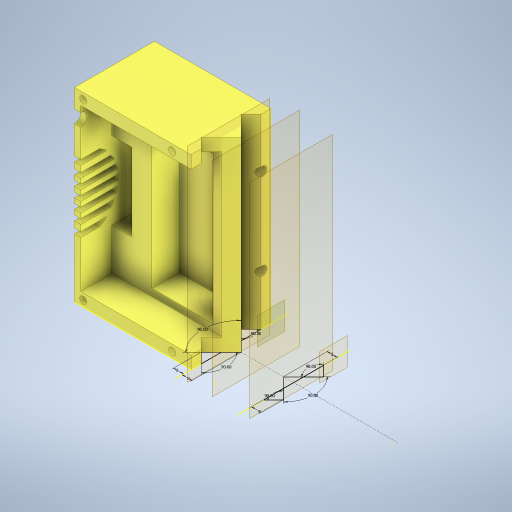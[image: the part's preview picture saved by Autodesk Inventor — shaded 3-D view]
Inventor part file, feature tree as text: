
AUTODESK INVENTOR PART (.ipt)
format: ipt  version: 2023 (Build 270158030, 158C)  size: 766,464 bytes
history: native  units: mm
features: sketch x21, extrude x18, hole x7, projected_geometry x7, plane x4, mirror x2, split x1
ambient origin geometry x8: Origin, YZ Plane, XZ Plane, XY Plane, X Axis, Y Axis, Z Axis, Center Point
bodies: Solid1 (feature_tree)
feature tree (60):
  extrude  "MainInnerBodyExtrusion"  Depth=149.0mm
  extrude  "HoleForCamerabase"  Depth=50.0mm
  extrude  "HoleForFan"  Depth=54.0mm
  extrude  "HoleForPi"  TaperAngle=0.0deg  [1 undecoded]
  extrude  "HoleForPoeAdapter"  Depth=62.0mm
  extrude  "HoleForThermister"  Depth=47.0mm
  extrude  "HoleForSensor"  Depth=32.0mm
  extrude  "SlotsForRearFan"  Depth=47.0mm
  extrude  "VentForCamera"  Depth=16.0mm
  extrude  "HoleForLens"  Depth=118.0mm
  sketch  "Sketch23"  dims[d26=49.0mm d27=118.0mm]
  hole  "Hole for 6-32 Insert"  [1 undecoded]
  hole  "Screw hole for 6-32 screw"  [1 undecoded]
  hole  "Side hole for 1-4 20 insert"  [1 undecoded]
  mirror  "Mirror for side insert"
  extrude  "Extrusion18"  Depth=17.0mm
  extrude  "HoleForPowerWire"  TaperAngle=0.0deg  [1 undecoded]
  extrude  "Extrusion22"  Depth=2.0mm
  extrude  "Extrusion23"  Depth=4.0mm
  extrude  "ExtrusionForBottom"  Depth=4.0mm
  hole  "1-4 holesToBoltFixture"  [1 undecoded]
  plane  "Work Plane1"
  plane  "Work Plane2"
  mirror  "Mirror4"
  extrude  "CutOutForFilter"  Depth=22.0mm
  hole  "Hole13"  [1 undecoded]
  plane  "Work Plane4"
  hole  "Hole14"  [1 undecoded]
  plane  "Work Plane5"
  hole  "Hole15"  [1 undecoded]
  split  "Split8"
  sketch  "Sketch46"  dims[d73=4.0mm d75=4.0mm]
  extrude  "Extrusion33"  Depth=149.0mm
  extrude  "Extrusion34"  Depth=149.0mm
  sketch  "Sketch1"  dims[d0=222.7mm d1=149.0mm]
  sketch  "Sketch3"  dims[d2=50.0mm d3=0.0mm d5=15.7mm]
  sketch  "Sketch4"  dims[d6=54.0mm d7=59.0mm]
  sketch  "Sketch6"  dims[d8=47.0mm d9=0.0mm]
  sketch  "Sketch7"  dims[d13=16.0mm d14=62.0mm]
  sketch  "Sketch11"  dims[d15=3.0mm d16=47.0mm]
  sketch  "Sketch15"  dims[d17=0.0mm d20=32.0mm]
  sketch  "Sketch16"  dims[d21=129.0mm d22=47.0mm]
  sketch  "Sketch18"  dims[d23=0.0mm d25=16.0mm]
  sketch  "Sketch24"  dims[d28=47.0mm d29=0.0mm]
  sketch  "Sketch25"  dims[d36=69.0mm d37=28.0mm]
  projected_geometry  "Projected Loop1"
  sketch  "Sketch26"  dims[d38=47.0mm d39=0.0mm]
  sketch  "Sketch37"  dims[d42=50.0mm d43=17.0mm]
  projected_geometry  "Projected Loop3"
  projected_geometry  "Projected Loop4"
  sketch  "Sketch39"  dims[d46=31.5mm d47=0.0mm]
  projected_geometry  "Projected Loop5"
  sketch  "Sketch40"  dims[d67=60.0mm d69=2.0mm]
  sketch  "Sketch43"  dims[d71=4.0mm d72=4.0mm]
  projected_geometry  "Projected Loop8"
  projected_geometry  "Projected Loop11"
  sketch  "Sketch47"  dims[d76=10.0mm d77=0.0mm d78=15.5mm]
  projected_geometry  "Projected Loop12"
  sketch  "Sketch48"  dims[d79=22.0mm d85=3.0mm]
  sketch  "Sketch50"  dims[d86=3.0mm d87=10.0mm d88=16.0mm d89=1.5mm d90=3.0mm d91=3.0mm d92=3.0mm d93=0.0mm d94=0.0mm d95=15.0mm d97=16.0mm d98=10.0mm d99=0.0mm d106=5.0mm d108=5.0mm d109=4.7mm d110=6.0mm d111=5.54mm d112=5.55mm d113=90.0deg d114=7.2mm d115=20.594885mm d116=3.797mm d117=6.0mm d118=12.7mm d119=2.362mm d120=90.0deg d121=15.0mm d122=20.594885mm d130=7.666mm d131=6.0mm d132=8.406mm d133=7.41mm d134=90.0deg d135=9.53mm d136=20.594885mm d137=24.0mm d138=10.0mm d139=3.0mm d140=25.0mm d141=0.0mm d142=30.0mm d144=10.0mm d145=0.0mm d222=76.2mm d223=76.2mm d224=76.2mm d225=76.2mm d226=25.0mm d227=111.350057mm d228=2.0mm d229=0.0mm d230=2.0mm d231=0.0mm d232=14.0mm d233=0.0mm d234=7.0mm d235=40.0mm d236=40.0mm d237=7.142mm d238=6.0mm d239=12.0mm d240=5.0mm d241=90.0deg d242=135.0mm d243=20.594885mm d246=30.0mm d247=-20.0mm d255=21.0mm d256=52.25mm d257=47.0mm d258=2.25mm d259=0.0mm d264=90.0deg d265=90.0deg d266=90.0deg d267=8.0mm d268=8.0mm d269=8.0mm d270=8.0mm d271=90.0deg d272=90.0deg d273=90.0deg d293=27.0mm d294=5.0mm d295=5.0mm d296=4.699mm d297=6.0mm d298=4.8514mm d299=5.55244mm d300=90.0deg d301=7.1374mm d302=0.0mm d307=8.0mm d308=6.0mm d309=9.52mm d310=9.9mm d311=90.0deg d312=12.75mm d313=0.0mm d314=8.0mm d315=6.0mm d316=9.52mm d317=9.9mm d318=90.0deg d319=12.75mm d320=0.0mm d321=149.0mm d322=0.0mm d323=149.0mm d324=0.0mm]
note: 9 required parameter values undecoded (feature->parameter linkage not recoverable at this tier; creation-order binding heuristic only, values carry confidence <= 0.55)
